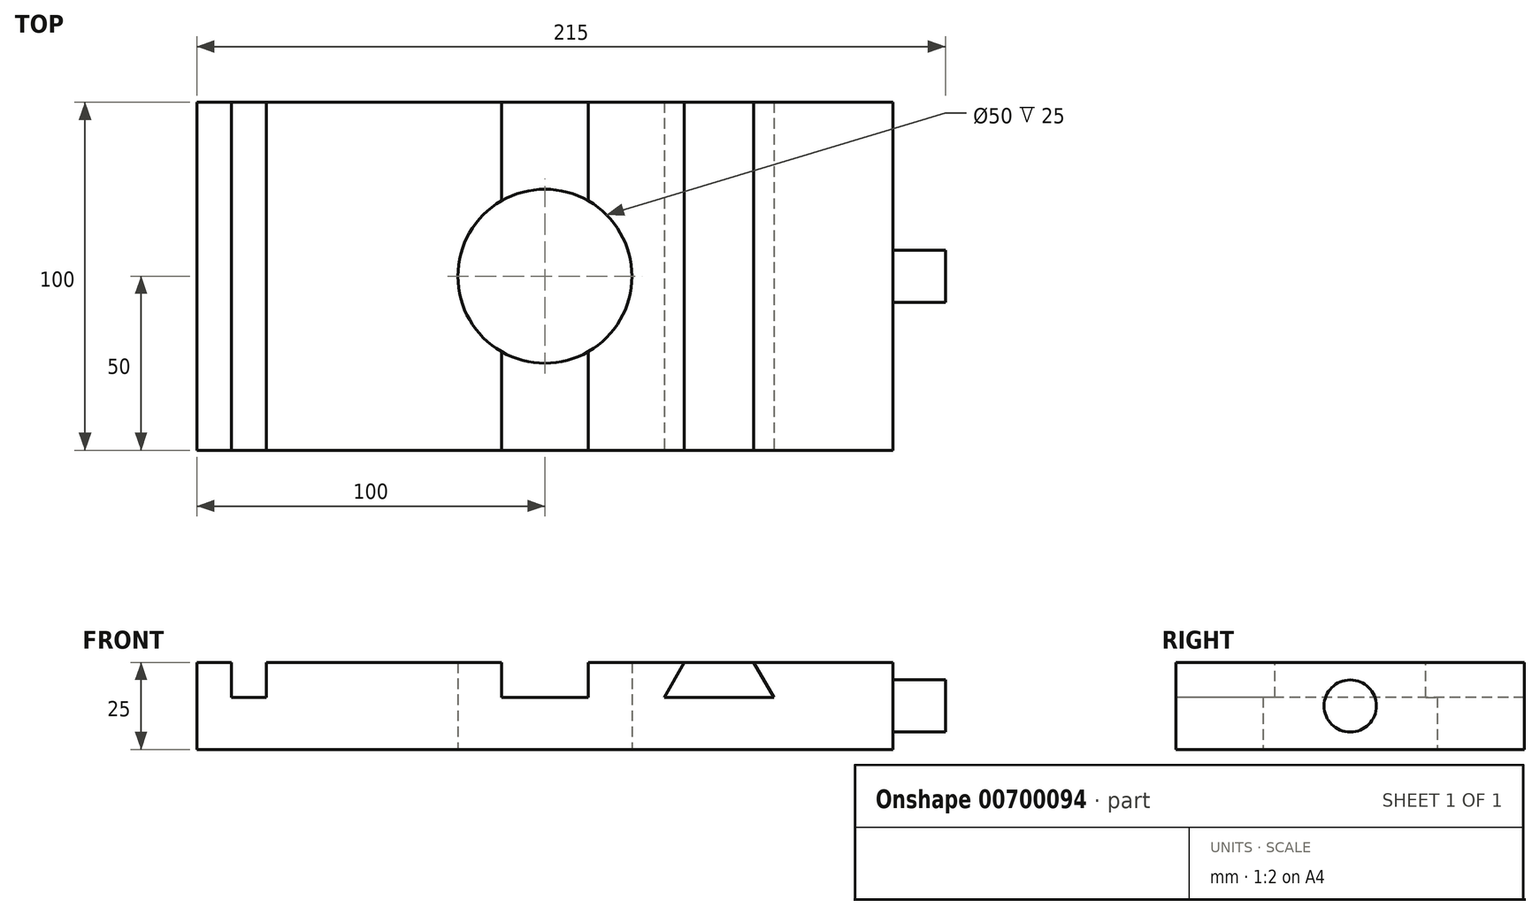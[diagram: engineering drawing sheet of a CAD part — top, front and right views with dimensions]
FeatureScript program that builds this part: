
annotation { "Feature Type Name" : "Feature", "Feature Type Description" : "" }
export const myFeature = defineFeature(function(context is Context, id is Id, definition is map)
    precondition{}
    {
        {
            var Q0;
            Q0=qCreatedBy(makeId("Top.planeOp"),FACE);
            var sketch = newSketch(context, id + "F0", { "sketchPlane" : qUnion([Q0])});
            skLineSegment(sketch, "E0.bottom", {"start": v(100, 50) * mm, "end": v(-100, 50) * mm});
            skLineSegment(sketch, "E0.top", {"start": v(100, -50) * mm, "end": v(-100, -50) * mm});
            skLineSegment(sketch, "E0.left", {"start": v(100, 50) * mm, "end": v(100, -50) * mm});
            skLineSegment(sketch, "E0.right", {"start": v(-100, 50) * mm, "end": v(-100, -50) * mm});
            skPoint(sketch, "E0.middle", {"position": v(0, 0) * mm});
            skCircle(sketch, "E1", {"center": v(0, 0) * mm, "radius": 25 * mm});
            skSolve(sketch);
        }
        {
            var Q0;
            Q0=makeQuery(id+"F0.imprint","IMPRINT",FACE,{"disambiguationData":[TD([[makeQuery(id+"F0.imprint","IMPRINT",EDGE,{"derivedFrom":sQuery(id+"F0.wireOp",EDGE,"E0.bottom")}),1.0]])]});
            extrude(context, id + "F1", {"entities" : qUnion([Q0]), "depth" : 25 * mm, "offsetDistance" : 25 * mm});
        }
        {
            var Q0;
            Q0=makeQuery(id+"F1.opExtrude","CAP_FACE",FACE,{"disambiguationData":[OSD([sQuery(id+"F0.wireOp",EDGE,"E0.bottom"),sQuery(id+"F0.wireOp",EDGE,"E0.top"),sQuery(id+"F0.wireOp",EDGE,"E0.left"),sQuery(id+"F0.wireOp",EDGE,"E0.right"),sQuery(id+"F0.wireOp",EDGE,"E1")])],"isStart":false});
            var sketch = newSketch(context, id + "F2", { "sketchPlane" : qUnion([Q0])});
            skLineSegment(sketch, "E2.bottom", {"start": v(-90, 50) * mm, "end": v(-80, 50) * mm});
            skLineSegment(sketch, "E2.top", {"start": v(-90, -50) * mm, "end": v(-80, -50) * mm});
            skLineSegment(sketch, "E2.left", {"start": v(-90, 50) * mm, "end": v(-90, -50) * mm});
            skLineSegment(sketch, "E2.right", {"start": v(-80, 50) * mm, "end": v(-80, -50) * mm});
            skLineSegment(sketch, "E3.bottom", {"start": v(-12.5, 50) * mm, "end": v(12.5, 50) * mm});
            skLineSegment(sketch, "E3.top", {"start": v(-12.5, -50) * mm, "end": v(12.5, -50) * mm});
            skLineSegment(sketch, "E3.left", {"start": v(-12.5, 50) * mm, "end": v(-12.5, -50) * mm});
            skLineSegment(sketch, "E3.right", {"start": v(12.5, 50) * mm, "end": v(12.5, -50) * mm});
            skPoint(sketch, "E4", {"position": v(0, 0) * mm});
            skLineSegment(sketch, "E5", {"start": v(0, 50) * mm, "end": v(0, -50) * mm, "construction": true});
            skSolve(sketch);
        }
        {
            var Q0;
            {var subQ0=sQuery(id+"F2.wireOp",EDGE,"E3.top");Q0=makeQuery(id+"F2.imprint","IMPRINT",FACE,{"disambiguationData":[TD([[makeQuery(id+"F2.imprint","IMPRINT",EDGE,{"derivedFrom":subQ0}),-1.0]])]});}
            var Q1;
            {var subQ0=sQuery(id+"F2.wireOp",EDGE,"E3.bottom");Q1=makeQuery(id+"F2.imprint","IMPRINT",FACE,{"disambiguationData":[TD([[makeQuery(id+"F2.imprint","IMPRINT",EDGE,{"derivedFrom":subQ0}),1.0]])]});}
            var Q2;
            Q2=makeQuery(id+"F2.imprint","IMPRINT",FACE,{"disambiguationData":[TD([[makeQuery(id+"F2.imprint","IMPRINT",EDGE,{"derivedFrom":sQuery(id+"F2.wireOp",EDGE,"E2.bottom")}),1.0]])]});
            extrude(context, id + "F3", {"entities" : qUnion([Q0, Q1, Q2]), "operationType" : NewBodyOperationType.REMOVE, "oppositeDirection" : true, "depth" : 10 * mm, "offsetDistance" : 25 * mm});
        }
        {
            var Q0;
            Q0=makeQuery(id+"F1.opExtrude","SWEPT_FACE",FACE,{"disambiguationData":[OSD([sQuery(id+"F0.wireOp",EDGE,"E0.top")])]});
            var sketch = newSketch(context, id + "F4", { "sketchPlane" : qUnion([Q0])});
            skLineSegment(sketch, "E6", {"start": v(40, 25) * mm, "end": v(34.23, 15) * mm});
            skLineSegment(sketch, "E7", {"start": v(34.23, 15) * mm, "end": v(65.77, 15) * mm});
            skLineSegment(sketch, "E8", {"start": v(65.77, 15) * mm, "end": v(60, 25) * mm});
            skLineSegment(sketch, "E9", {"start": v(50, 15) * mm, "end": v(50, 25) * mm, "construction": true});
            skSolve(sketch);
        }
        {
            var Q0;
            {var subQ0=sQuery(id+"F4.wireOp",EDGE,"E6");Q0=makeQuery(id+"F4.imprint","IMPRINT",FACE,{"disambiguationData":[TD([[makeQuery(id+"F4.imprint","IMPRINT",EDGE,{"derivedFrom":subQ0}),1.0]])]});}
            extrude(context, id + "F5", {"entities" : qUnion([Q0]), "operationType" : NewBodyOperationType.REMOVE, "oppositeDirection" : true, "depth" : 100 * mm, "offsetDistance" : 25 * mm});
        }
        {
            var Q0;
            Q0=makeQuery(id+"F1.opExtrude","SWEPT_FACE",FACE,{"disambiguationData":[OSD([sQuery(id+"F0.wireOp",EDGE,"E0.left")])]});
            var sketch = newSketch(context, id + "F6", { "sketchPlane" : qUnion([Q0])});
            skCircle(sketch, "E10", {"center": v(0, 12.5) * mm, "radius": 7.5 * mm});
            skPoint(sketch, "E10.centerSnap0", {"position": v(-50, 12.5) * mm});
            skPoint(sketch, "E10.centerSnap1", {"position": v(0, 25) * mm});
            skSolve(sketch);
        }
        {
            var Q0;
            Q0=makeQuery(id+"F6.imprint","IMPRINT",FACE,{"disambiguationData":[TD([[makeQuery(id+"F6.imprint","IMPRINT",EDGE,{"derivedFrom":sQuery(id+"F6.wireOp",EDGE,"E10")}),1.0]])]});
            extrude(context, id + "F7", {"entities" : qUnion([Q0]), "operationType" : NewBodyOperationType.ADD, "depth" : 15 * mm, "offsetDistance" : 25 * mm});
        }
        {
            var Q0;
            Q0=makeQuery(id+"F1.opExtrude","SWEPT_FACE",FACE,{"disambiguationData":[OSD([sQuery(id+"F0.wireOp",EDGE,"E0.top")])]});
            var sketch = newSketch(context, id + "F8", { "sketchPlane" : qUnion([Q0])});
            skLineSegment(sketch, "E11", {"start": v(40, 25) * mm, "end": v(60, 25) * mm});
            skLineSegment(sketch, "E12", {"start": v(60, 25) * mm, "end": v(65.77, 15) * mm});
            skLineSegment(sketch, "E13", {"start": v(65.77, 15) * mm, "end": v(34.23, 15) * mm});
            skLineSegment(sketch, "E14", {"start": v(34.23, 15) * mm, "end": v(40, 25) * mm});
            skSolve(sketch);
        }
        {
            var Q0;
            Q0 = qSketchRegion(id + "F8", true);
            extrude(context, id + "F9", {"entities" : qUnion([Q0]), "oppositeDirection" : true, "depth" : 100 * mm, "offsetDistance" : 25 * mm});
        }
    });
